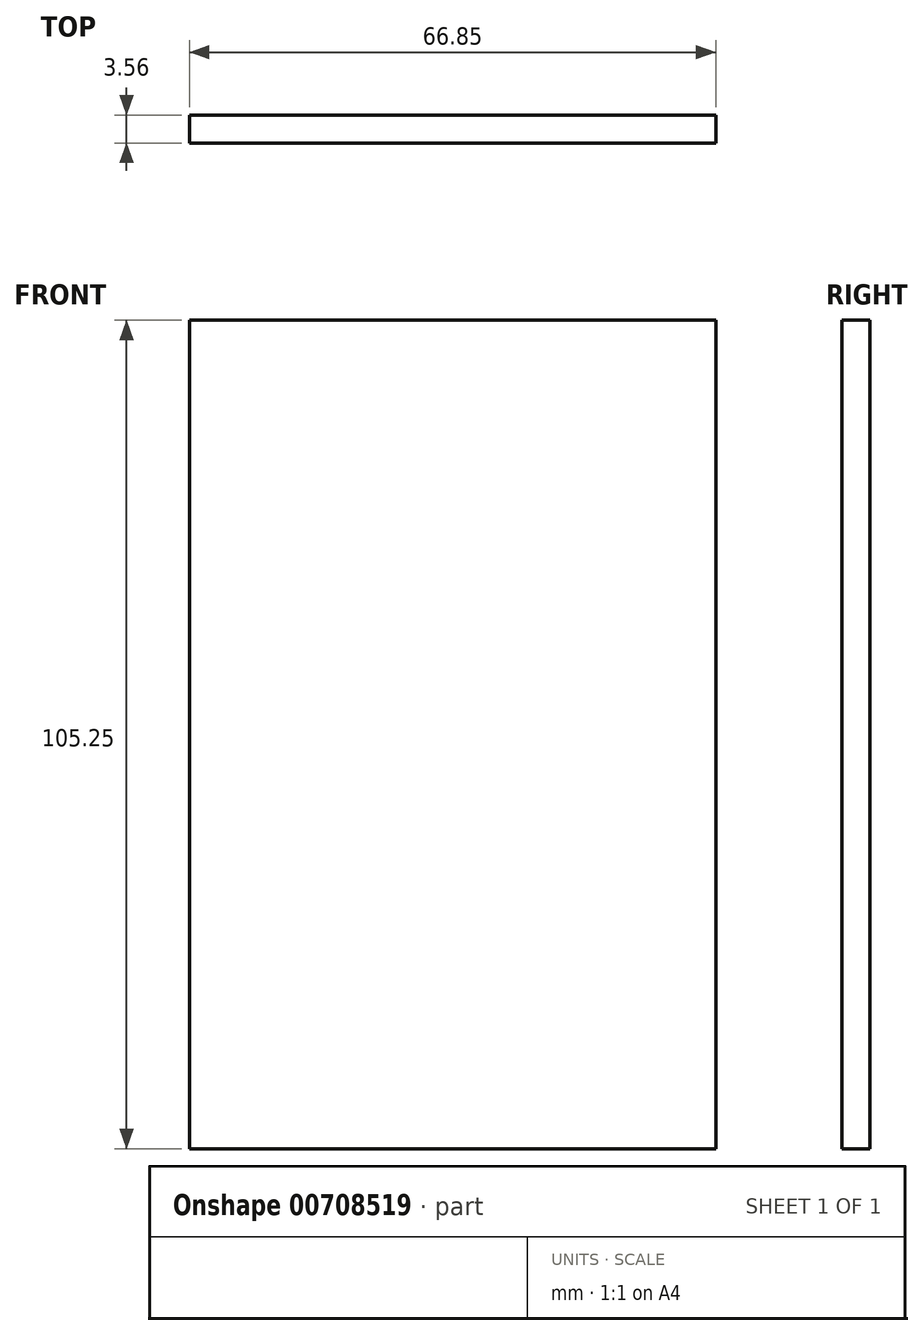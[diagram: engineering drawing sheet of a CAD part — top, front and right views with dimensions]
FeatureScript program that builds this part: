
annotation { "Feature Type Name" : "Feature", "Feature Type Description" : "" }
export const myFeature = defineFeature(function(context is Context, id is Id, definition is map)
    precondition{}
    {
        {
            var Q0;
            Q0=qCreatedBy(makeId("Front.planeOp"),FACE);
            var sketch = newSketch(context, id + "F0", { "sketchPlane" : qUnion([Q0])});
            skLineSegment(sketch, "E0.bottom", {"start": v(-45.24, 38.26) * mm, "end": v(21.61, 38.26) * mm});
            skLineSegment(sketch, "E0.top", {"start": v(-45.24, -66.99) * mm, "end": v(21.61, -66.99) * mm});
            skLineSegment(sketch, "E0.left", {"start": v(-45.24, 38.26) * mm, "end": v(-45.24, -66.99) * mm});
            skLineSegment(sketch, "E0.right", {"start": v(21.61, 38.26) * mm, "end": v(21.61, -66.99) * mm});
            skSolve(sketch);
        }
        {
            var Q0;
            Q0=makeQuery(id+"F0.imprint","IMPRINT",FACE,{"disambiguationData":[TD([[makeQuery(id+"F0.imprint","IMPRINT",EDGE,{"derivedFrom":sQuery(id+"F0.wireOp",EDGE,"E0.bottom")}),-1.0]])]});
            extrude(context, id + "F1", {"entities" : qUnion([Q0]), "depth" : 3.56 * mm, "offsetDistance" : 25.4 * mm});
        }
    });
